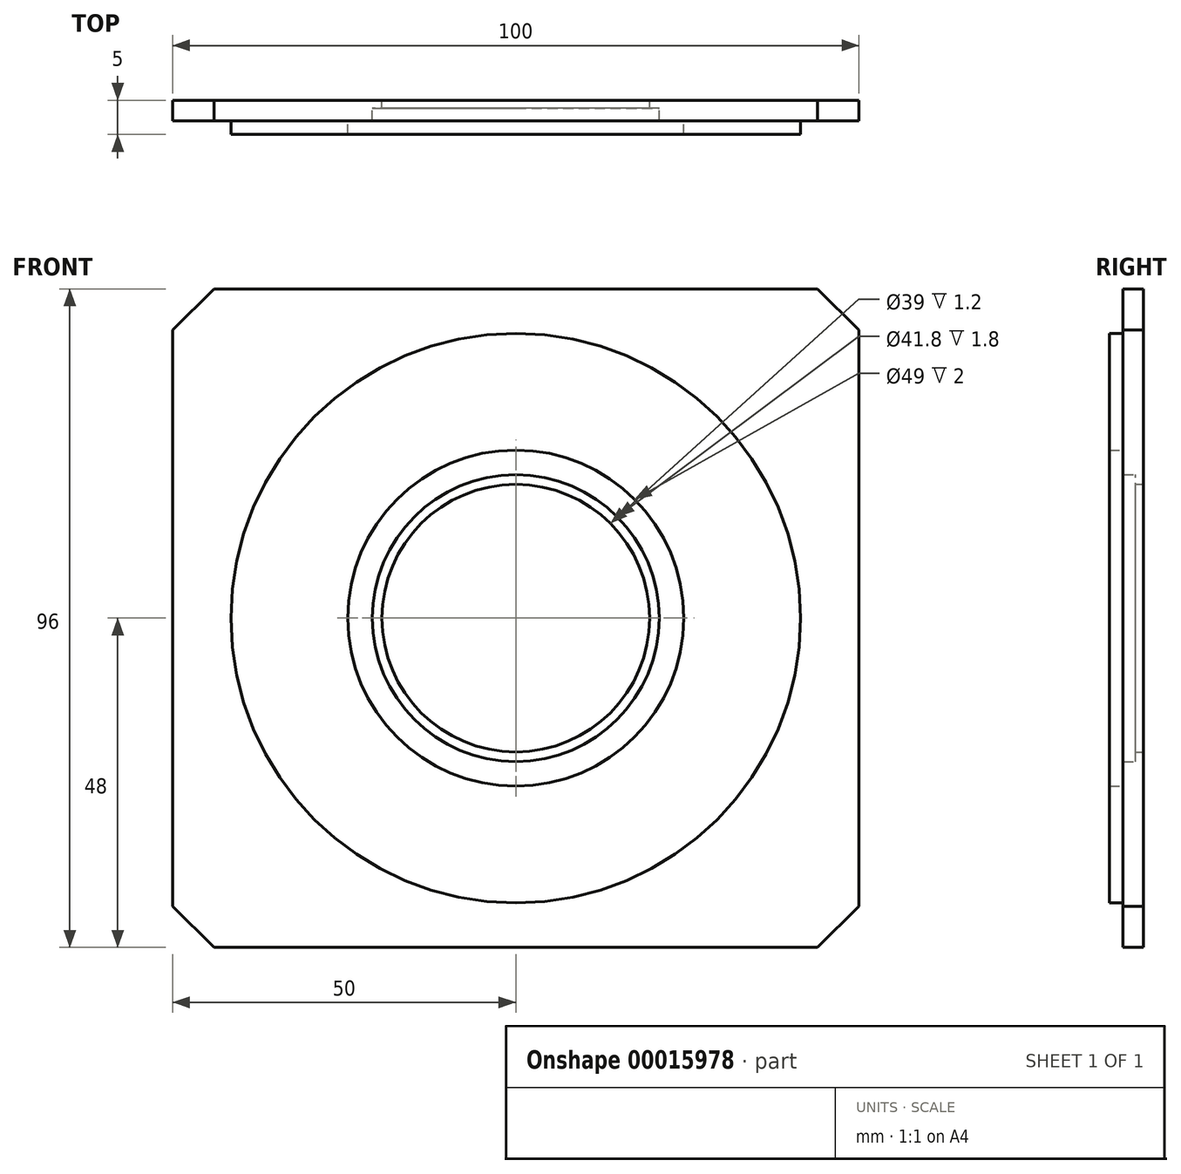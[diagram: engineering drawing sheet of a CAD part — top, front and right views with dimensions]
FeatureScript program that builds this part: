
annotation { "Feature Type Name" : "Feature", "Feature Type Description" : "" }
export const myFeature = defineFeature(function(context is Context, id is Id, definition is map)
    precondition{}
    {
        {
            var Q0;
            Q0=qCreatedBy(makeId("Front.planeOp"),FACE);
            var sketch = newSketch(context, id + "F0", { "sketchPlane" : qUnion([Q0])});
            skCircle(sketch, "E0", {"center": v(0, 0) * mm, "radius": 19.5 * mm});
            skLineSegment(sketch, "E1.bottom", {"start": v(-50, 48) * mm, "end": v(50, 48) * mm});
            skLineSegment(sketch, "E1.top", {"start": v(-50, -48) * mm, "end": v(50, -48) * mm});
            skLineSegment(sketch, "E1.left", {"start": v(-50, 48) * mm, "end": v(-50, -48) * mm});
            skLineSegment(sketch, "E1.right", {"start": v(50, 48) * mm, "end": v(50, -48) * mm});
            skSolve(sketch);
        }
        {
            var Q0;
            Q0 = qSketchRegion(id + "F0", true);
            extrude(context, id + "F1", {"entities" : qUnion([Q0]), "depth" : 1.2 * mm});
        }
        {
            var Q0;
            Q0=makeQuery(id+"F1.opExtrude","CAP_FACE",FACE,{"disambiguationData":[OSD([sQuery(id+"F0.wireOp",EDGE,"E0"),sQuery(id+"F0.wireOp",EDGE,"E1.bottom"),sQuery(id+"F0.wireOp",EDGE,"E1.top"),sQuery(id+"F0.wireOp",EDGE,"E1.left"),sQuery(id+"F0.wireOp",EDGE,"E1.right")])],"isStart":false});
            var sketch = newSketch(context, id + "F2", { "sketchPlane" : qUnion([Q0])});
            skCircle(sketch, "E2", {"center": v(0, 0) * mm, "radius": 20.9 * mm});
            skSolve(sketch);
        }
        {
            var Q0;
            Q0=makeQuery(id+"F2.imprint","IMPRINT",FACE,{"disambiguationData":[TD([[makeQuery(id+"F2.imprint","IMPRINT",EDGE,{"derivedFrom":sQuery(id+"F2.wireOp",EDGE,"E2")}),-1.0]])]});
            extrude(context, id + "F3", {"entities" : qUnion([Q0]), "operationType" : NewBodyOperationType.ADD, "depth" : 1.8 * mm});
        }
        {
            var Q0;
            Q0=qCreatedBy(makeId("Front.planeOp"),FACE);
            var sketch = newSketch(context, id + "F4", { "sketchPlane" : qUnion([Q0])});
            skCircle(sketch, "E3", {"center": v(0, 0) * mm, "radius": 41.5 * mm});
            skCircle(sketch, "E4", {"center": v(0, 0) * mm, "radius": 24.5 * mm});
            skSolve(sketch);
        }
        {
            var Q0;
            Q0=makeQuery(id+"F4.imprint","IMPRINT",FACE,{"disambiguationData":[TD([[makeQuery(id+"F4.imprint","IMPRINT",EDGE,{"derivedFrom":sQuery(id+"F4.wireOp",EDGE,"E3")}),1.0]])]});
            extrude(context, id + "F5", {"entities" : qUnion([Q0]), "operationType" : NewBodyOperationType.ADD, "depth" : 5 * mm});
        }
        {
            var Q0;
            {var subQ0=sQuery(id+"F0.wireOp",EDGE,"E1.bottom");var subQ1=sQuery(id+"F0.wireOp",EDGE,"E1.right");Q0=makeQuery(id+"F3.boolean.opBoolean","MERGE",EDGE,{"derivedFrom":[makeQuery(id+"F1.opExtrude","SWEPT_EDGE",EDGE,{"disambiguationData":[OSD([subQ0,subQ1])]}),makeQuery(id+"F3.opExtrude","SWEPT_EDGE",EDGE,{"disambiguationData":[OSD([subQ0,subQ1])]})]});}
            chamfer(context, id + "F6", {"entities" : qUnion([Q0]), "width" : 6 * mm, "tangentPropagation" : true});
        }
        {
            var Q0;
            {var subQ0=sQuery(id+"F0.wireOp",EDGE,"E1.top");var subQ1=sQuery(id+"F0.wireOp",EDGE,"E1.right");Q0=makeQuery(id+"F3.boolean.opBoolean","MERGE",EDGE,{"derivedFrom":[makeQuery(id+"F1.opExtrude","SWEPT_EDGE",EDGE,{"disambiguationData":[OSD([subQ0,subQ1])]}),makeQuery(id+"F3.opExtrude","SWEPT_EDGE",EDGE,{"disambiguationData":[OSD([subQ0,subQ1])]})]});}
            var Q1;
            {var subQ0=sQuery(id+"F0.wireOp",EDGE,"E1.top");var subQ1=sQuery(id+"F0.wireOp",EDGE,"E1.left");Q1=makeQuery(id+"F3.boolean.opBoolean","MERGE",EDGE,{"derivedFrom":[makeQuery(id+"F1.opExtrude","SWEPT_EDGE",EDGE,{"disambiguationData":[OSD([subQ0,subQ1])]}),makeQuery(id+"F3.opExtrude","SWEPT_EDGE",EDGE,{"disambiguationData":[OSD([subQ0,subQ1])]})]});}
            var Q2;
            {var subQ0=sQuery(id+"F0.wireOp",EDGE,"E1.bottom");var subQ1=sQuery(id+"F0.wireOp",EDGE,"E1.left");Q2=makeQuery(id+"F3.boolean.opBoolean","MERGE",EDGE,{"derivedFrom":[makeQuery(id+"F1.opExtrude","SWEPT_EDGE",EDGE,{"disambiguationData":[OSD([subQ0,subQ1])]}),makeQuery(id+"F3.opExtrude","SWEPT_EDGE",EDGE,{"disambiguationData":[OSD([subQ0,subQ1])]})]});}
            chamfer(context, id + "F7", {"entities" : qUnion([Q0, Q1, Q2]), "width" : 6 * mm, "tangentPropagation" : true});
        }
    });
